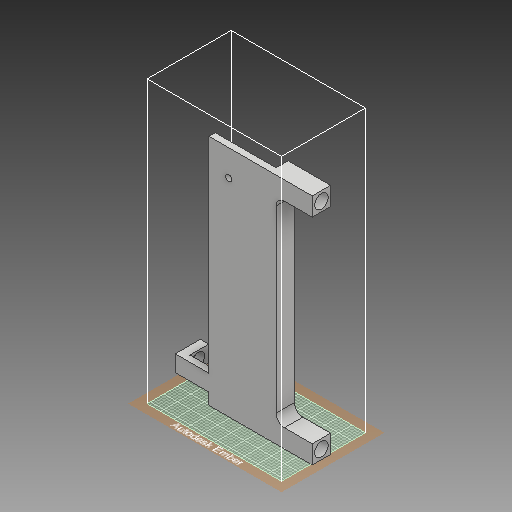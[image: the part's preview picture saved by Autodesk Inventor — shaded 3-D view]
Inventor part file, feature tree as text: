
AUTODESK INVENTOR PART (.ipt)
format: ipt  version: 2018 (Build 220112000, 112)  size: 562,176 bytes
history: native  units: mm
features: sketch x32, extrude x25, fillet x2
ambient origin geometry x8: Origin, YZ Plane, XZ Plane, XY Plane, X Axis, Y Axis, Z Axis, Center Point
bodies: Solid1 (feature_tree)
feature tree (59):
  extrude  "Extrusion1"  Depth=5.5118mm
  extrude  "Extrusion2"  Depth=8.763mm
  fillet  "Fillet1"  Radius=8.763mm
  sketch  "Sketch3"  dims[d5=5.5118mm d6=5.588mm]
  extrude  "Extrusion3"  Depth=5.5118mm
  extrude  "Extrusion4"  Depth=30.0mm TaperAngle=0.0deg
  sketch  "Sketch6"  dims[d13=3.0mm d14=18.97mm d15=0.0mm]
  extrude  "Extrusion5"  Depth=5.0mm
  extrude  "Extrusion6"  Depth=3.0mm TaperAngle=0.0deg
  sketch  "Sketch9"  dims[d21=0.0mm d22=0.0mm]
  extrude  "Extrusion7"  Depth=6.985mm
  extrude  "Extrusion8"  Depth=5.0mm TaperAngle=0.0deg
  extrude  "Extrusion9"  TaperAngle=0.0deg  [1 undecoded]
  extrude  "Extrusion10"  TaperAngle=0.0deg  [1 undecoded]
  sketch  "Sketch14"  dims[d37=3.875mm d38=6.2mm]
  sketch  "Sketch15"  dims[d39=5.0mm d40=0.0mm d41=10.0mm]
  extrude  "Extrusion11"  Depth=9.0mm
  extrude  "Extrusion12"  Depth=3.0mm TaperAngle=0.0deg
  extrude  "Extrusion13"  Depth=3.0mm TaperAngle=0.0deg
  extrude  "Extrusion14"  Depth=6.2mm
  extrude  "Extrusion15"  Depth=10.0mm
  extrude  "Extrusion16"  Depth=13.0mm TaperAngle=0.0deg
  extrude  "Extrusion17"  Depth=3.0mm TaperAngle=0.0deg
  sketch  "Sketch23"  dims[d66=30.0mm d67=0.0mm d68=100.0mm]
  extrude  "Extrusion18"  Depth=4.375mm
  extrude  "Extrusion19"  Depth=3.0mm
  extrude  "Extrusion20"  Depth=9.485mm
  sketch  "Sketch27"  dims[d78=7.75mm]
  extrude  "Extrusion21"  Depth=3.0mm
  fillet  "Fillet2"  Radius=3.0mm
  extrude  "Extrusion22"  Depth=3.0mm TaperAngle=0.0deg
  extrude  "Extrusion23"  Depth=100.0mm
  extrude  "Extrusion24"  Depth=7.75mm
  extrude  "Extrusion25"  Depth=4.0mm
  sketch  "Sketch1"  dims[d0=8.763mm d1=5.5118mm]
  sketch  "Sketch2"  dims[d2=5.588mm d3=2.3368mm d4=8.763mm]
  sketch  "Sketch4"  dims[d7=2.3368mm d8=30.0mm d9=0.0mm]
  sketch  "Sketch5"  dims[d10=0.25mm d11=0.0mm d12=5.0mm]
  sketch  "Sketch7"  dims[d16=9.485mm d17=6.985mm]
  sketch  "Sketch8"  dims[d18=3.175mm d19=5.0mm d20=0.0mm]
  sketch  "Sketch10"  dims[d23=0.0mm d26=0.0mm]
  sketch  "Sketch11"  dims[d27=0.0mm d28=9.0mm]
  sketch  "Sketch12"  dims[d29=7.75mm d30=3.0mm d31=0.0mm]
  sketch  "Sketch13"  dims[d32=4.0mm d33=8.0mm d34=3.0mm d35=0.0mm d36=0.0mm]
  sketch  "Sketch16"  dims[d42=10.0mm d43=0.0mm d44=13.0mm d45=0.0mm]
  sketch  "Sketch17"  dims[d46=3.0mm d47=8.75mm d48=0.0mm]
  sketch  "Sketch18"  dims[d49=0.0mm d52=4.375mm]
  sketch  "Sketch19"  dims[d53=4.375mm d54=3.0mm]
  sketch  "Sketch20"  dims[d55=2.0mm d56=0.0mm d57=9.485mm]
  sketch  "Sketch21"  dims[d58=6.985mm d59=6.985mm d60=3.0mm]
  sketch  "Sketch22"  dims[d61=3.0mm d62=0.0mm d63=3.0mm d64=0.0mm]
  sketch  "Sketch24"  dims[d69=12.042mm d70=7.75mm]
  sketch  "Sketch25"  dims[d71=3.0mm d72=0.0mm d73=4.0mm]
  sketch  "Sketch26"  dims[d74=9.0mm d75=3.0mm d76=0.0mm d77=0.0mm]
  sketch  "Sketch28"  dims[d79=3.875mm]
  sketch  "Sketch29"  dims[d80=3.875mm]
  sketch  "Sketch30"  dims[d81=6.2mm]
  sketch  "Sketch31"  dims[d82=4.0mm d83=0.0mm]
  sketch  "Sketch32"  dims[d84=5.512mm d85=4.375mm d86=4.375mm d87=3.0mm d88=3.0mm d89=0.0mm d90=2.0mm d91=0.0mm d92=8.763mm d93=8.763mm d94=20.25mm d95=0.0mm d96=6.5mm d97=6.5mm d98=17.25mm d99=0.0mm d100=4.0mm d101=2.75mm d102=100.0mm d103=0.0mm d104=100.0mm d105=98.425mm d106=44.45mm d107=44.45mm d108=10.0mm d109=10.0mm d110=10.0mm d111=5.0mm d112=0.0mm d113=20.0mm d114=2.75mm d115=0.0mm d116=20.0mm d117=0.0mm]
note: 2 required parameter values undecoded (feature->parameter linkage not recoverable at this tier; creation-order binding heuristic only, values carry confidence <= 0.55)
